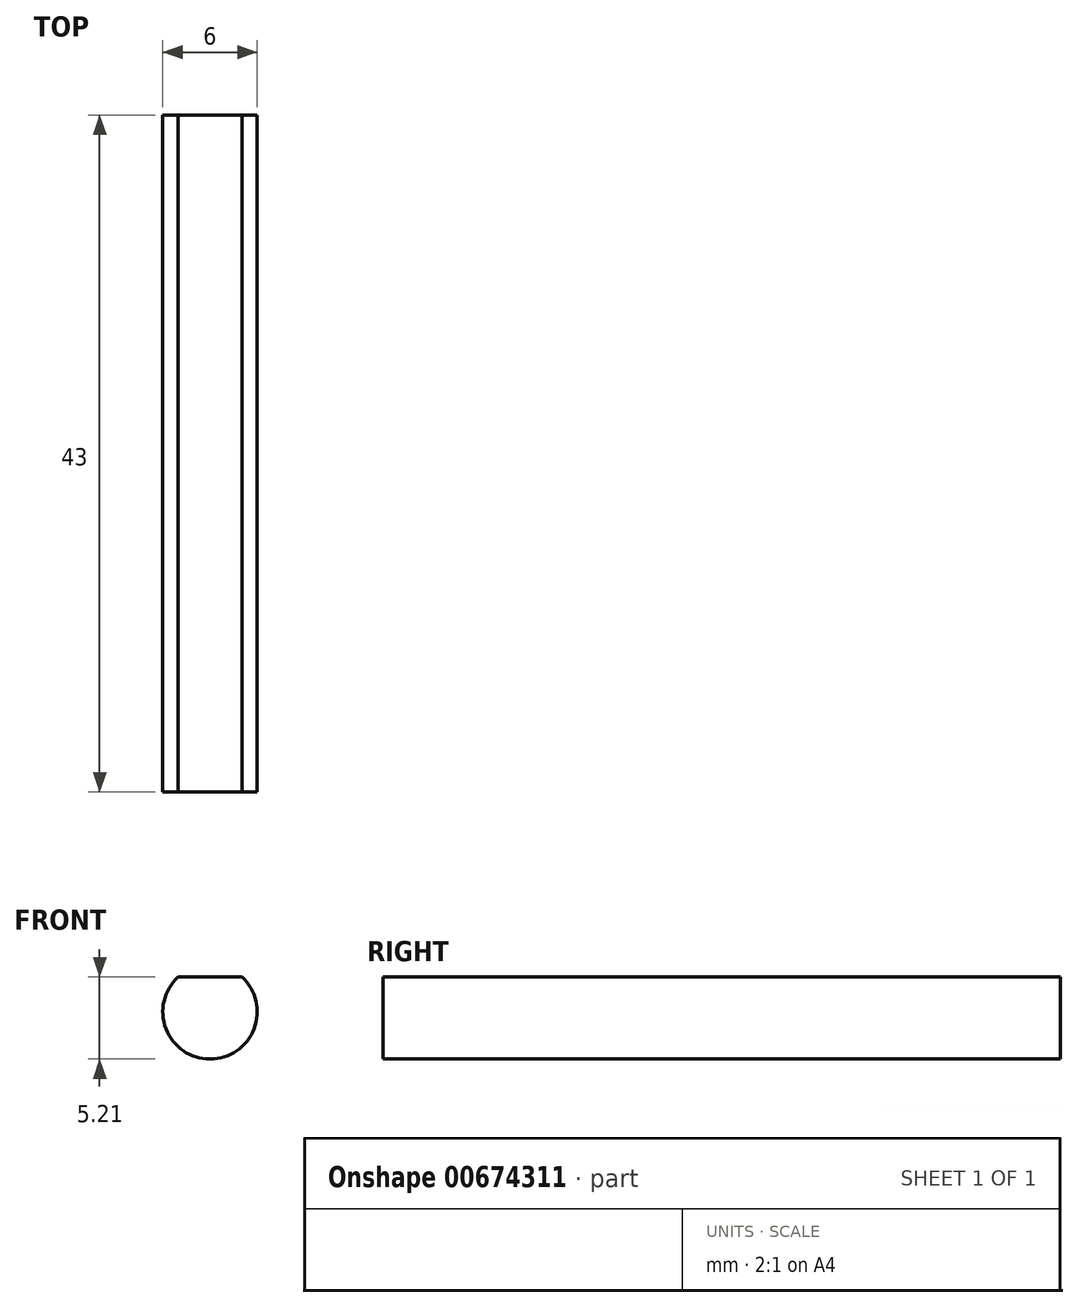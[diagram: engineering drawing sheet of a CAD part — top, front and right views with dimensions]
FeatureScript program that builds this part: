
annotation { "Feature Type Name" : "Feature", "Feature Type Description" : "" }
export const myFeature = defineFeature(function(context is Context, id is Id, definition is map)
    precondition{}
    {
        {
            var Q0;
            Q0=qCreatedBy(makeId("Front.planeOp"),FACE);
            var sketch = newSketch(context, id + "F0", { "sketchPlane" : qUnion([Q0])});
            skCircle(sketch, "E0", {"center": v(0, 0) * mm, "radius": 3 * mm});
            skSolve(sketch);
        }
        {
            var Q0;
            Q0 = qSketchRegion(id + "F0", true);
            extrude(context, id + "F1", {"entities" : qUnion([Q0]), "depth" : 43 * mm, "offsetDistance" : 25 * mm});
        }
        {
            var Q0;
            Q0=makeQuery(id+"F1.opExtrude","CAP_FACE",FACE,{"disambiguationData":[OSD([sQuery(id+"F0.wireOp",EDGE,"E0")])],"isStart":false});
            var sketch = newSketch(context, id + "F2", { "sketchPlane" : qUnion([Q0])});
            skLineSegment(sketch, "E1.bottom", {"start": v(-2.03, 3.43) * mm, "end": v(2.03, 3.43) * mm});
            skLineSegment(sketch, "E1.top", {"start": v(-2.03, 2.2) * mm, "end": v(2.03, 2.2) * mm});
            skLineSegment(sketch, "E1.left", {"start": v(-2.03, 3.43) * mm, "end": v(-2.03, 2.2) * mm});
            skLineSegment(sketch, "E1.right", {"start": v(2.03, 3.43) * mm, "end": v(2.03, 2.2) * mm});
            skSolve(sketch);
        }
        {
            var Q0;
            Q0 = qSketchRegion(id + "F2", true);
            extrude(context, id + "F3", {"entities" : qUnion([Q0]), "operationType" : NewBodyOperationType.REMOVE, "endBound" : BoundingType.THROUGH_ALL, "oppositeDirection" : true, "depth" : 25 * mm, "offsetDistance" : 25 * mm});
        }
    });
